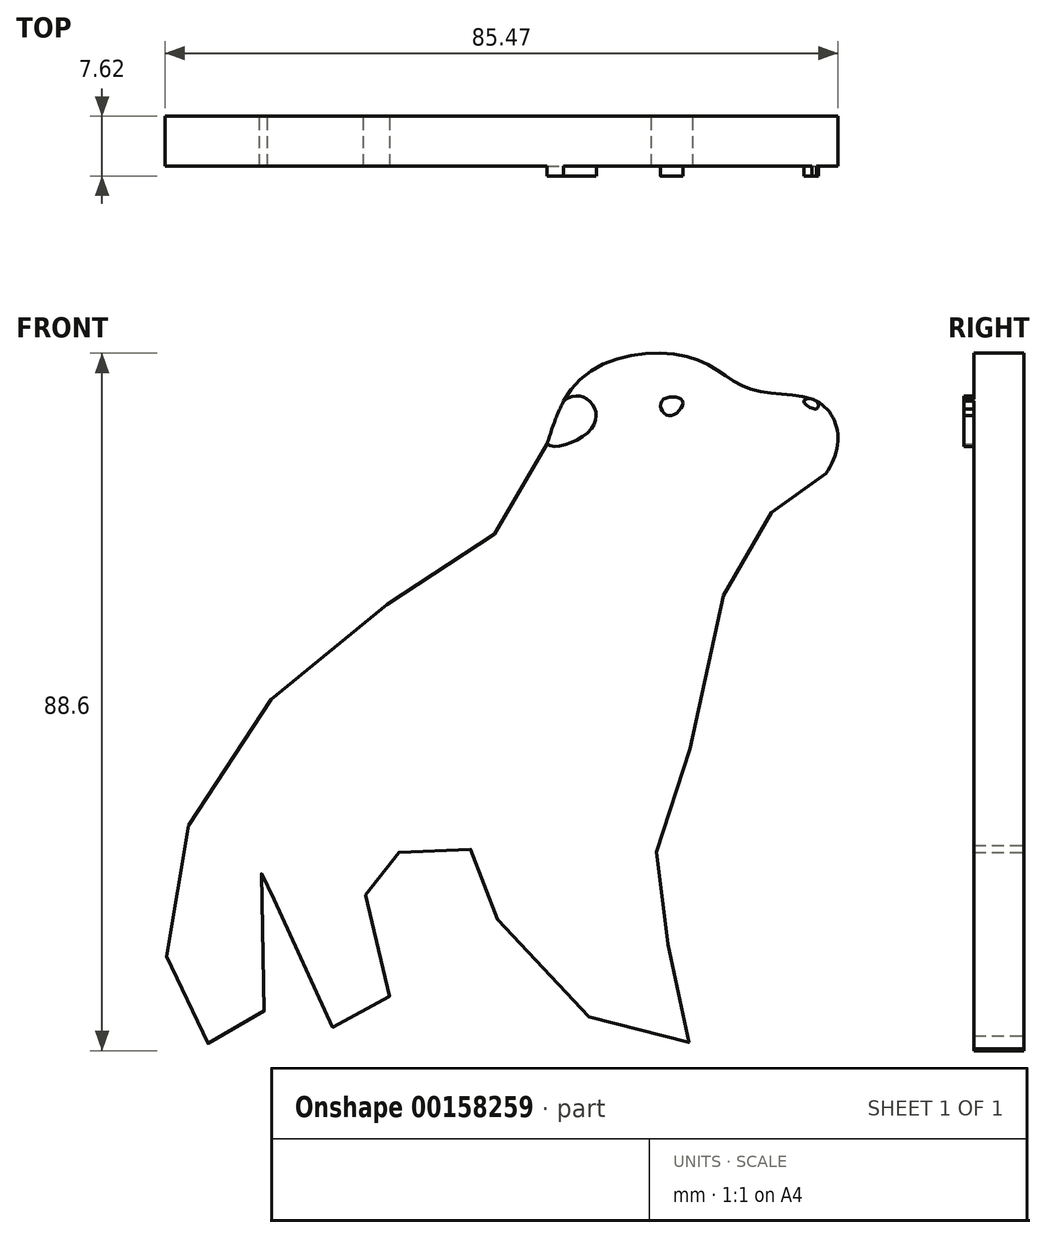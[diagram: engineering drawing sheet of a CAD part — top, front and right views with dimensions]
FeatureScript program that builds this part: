
annotation { "Feature Type Name" : "Feature", "Feature Type Description" : "" }
export const myFeature = defineFeature(function(context is Context, id is Id, definition is map)
    precondition{}
    {
        {
            var Q0;
            Q0=qCreatedBy(makeId("Front.planeOp"),FACE);
            var sketch = newSketch(context, id + "F0", { "sketchPlane" : qUnion([Q0])});
            skFitSpline(sketch, "E0", {"points": [v(-4.04, 31.74) * mm, v(-11.37, 35.69) * mm, v(-25.83, 32.87) * mm, v(-33.16, 17.1) * mm, v(-56.63, 0) * mm, v(-77.86, -31.55) * mm, v(-73.46, -51.04) * mm, v(-66.47, -49.6) * mm, v(-66.34, -27.14) * mm, v(-56.84, -49.54) * mm, v(-49.95, -45.95) * mm, v(-53.13, -29.76) * mm, v(-47.24, -26.86) * mm, v(-39.03, -27.09) * mm, v(-34, -39.82) * mm, v(-12, -51.42) * mm, v(-16.4, -32.9) * mm, v(-13.44, -20.66) * mm, v(-4.42, 13.34) * mm, v(2.34, 17.84) * mm, v(7.04, 24.8) * mm, v(4.31, 30.24) * mm, v(-4.04, 31.74) * mm]});
            skFitSpline(sketch, "E1", {"points": [v(-15.3, 30.24) * mm, v(-14.37, 28.36) * mm, v(-12.68, 30.24) * mm, v(-15.3, 30.24) * mm]});
            skFitSpline(sketch, "E2", {"points": [v(4.31, 30.24) * mm, v(2.72, 30.24) * mm, v(4.31, 29.24) * mm, v(4.31, 30.24) * mm]});
            skFitSpline(sketch, "E3", {"points": [v(-24.51, 30.24) * mm, v(-27.77, 30.24) * mm, v(-29.88, 24.8) * mm, v(-24.13, 26.86) * mm, v(-24.51, 30.24) * mm]});
            skFitSpline(sketch, "E4", {"points": [v(5.54, 21) * mm, v(0, 20.93) * mm, v(-2.21, 21.81) * mm], "startDerivative": vector(-10.05, -1.1) * mm, "endDerivative": vector(-4.86, 2.73) * mm});
            skPoint(sketch, "E5", {"position": v(-31.8, -42.39) * mm});
            skPoint(sketch, "E6", {"position": v(-28.25, -45.51) * mm});
            skPoint(sketch, "E7", {"position": v(-22.67, -49.13) * mm});
            skSolve(sketch);
        }
        {
            var Q0;
            Q0=makeQuery(id+"F0.imprint","IMPRINT",FACE,{"disambiguationData":[TD([[makeQuery(id+"F0.imprint","IMPRINT",EDGE,{"derivedFrom":sQuery(id+"F0.wireOp",EDGE,"E1")}),-1.0]])]});
            extrude(context, id + "F1", {"entities" : qUnion([Q0]), "depth" : 6.35 * mm});
        }
        {
            var Q0;
            {var subQ0=sQuery(id+"F0.wireOp",EDGE,"E3");var subQ1=sQuery(id+"F0.wireOp",EDGE,"E0");var subQ2=makeQuery(id+"F0.imprint","INTERSECT",VERTEX,{"disambiguationData":[OD(0.0)],"derivedFrom":[subQ1,subQ0]});Q0=makeQuery(id+"F0.imprint","IMPRINT",FACE,{"disambiguationData":[TD([[makeQuery(id+"F0.imprint","IMPRINT",EDGE,{"disambiguationData":[TD([[subQ2,1.0]])],"derivedFrom":subQ1}),1.0]])]});}
            var Q1;
            Q1=makeQuery(id+"F0.imprint","IMPRINT",FACE,{"disambiguationData":[TD([[makeQuery(id+"F0.imprint","IMPRINT",EDGE,{"derivedFrom":sQuery(id+"F0.wireOp",EDGE,"E1")}),1.0]])]});
            var Q2;
            {var subQ0=sQuery(id+"F0.wireOp",EDGE,"E2");var subQ1=sQuery(id+"F0.wireOp",EDGE,"E0");var subQ2=makeQuery(id+"F0.imprint","INTERSECT",VERTEX,{"disambiguationData":[OD(0.0)],"derivedFrom":[subQ1,subQ0]});Q2=makeQuery(id+"F0.imprint","IMPRINT",FACE,{"disambiguationData":[TD([[makeQuery(id+"F0.imprint","IMPRINT",EDGE,{"disambiguationData":[TD([[subQ2,-1.0]])],"derivedFrom":subQ1}),1.0]])]});}
            extrude(context, id + "F2", {"entities" : qUnion([Q0, Q1, Q2]), "operationType" : NewBodyOperationType.ADD, "depth" : 7.62 * mm});
        }
    });
